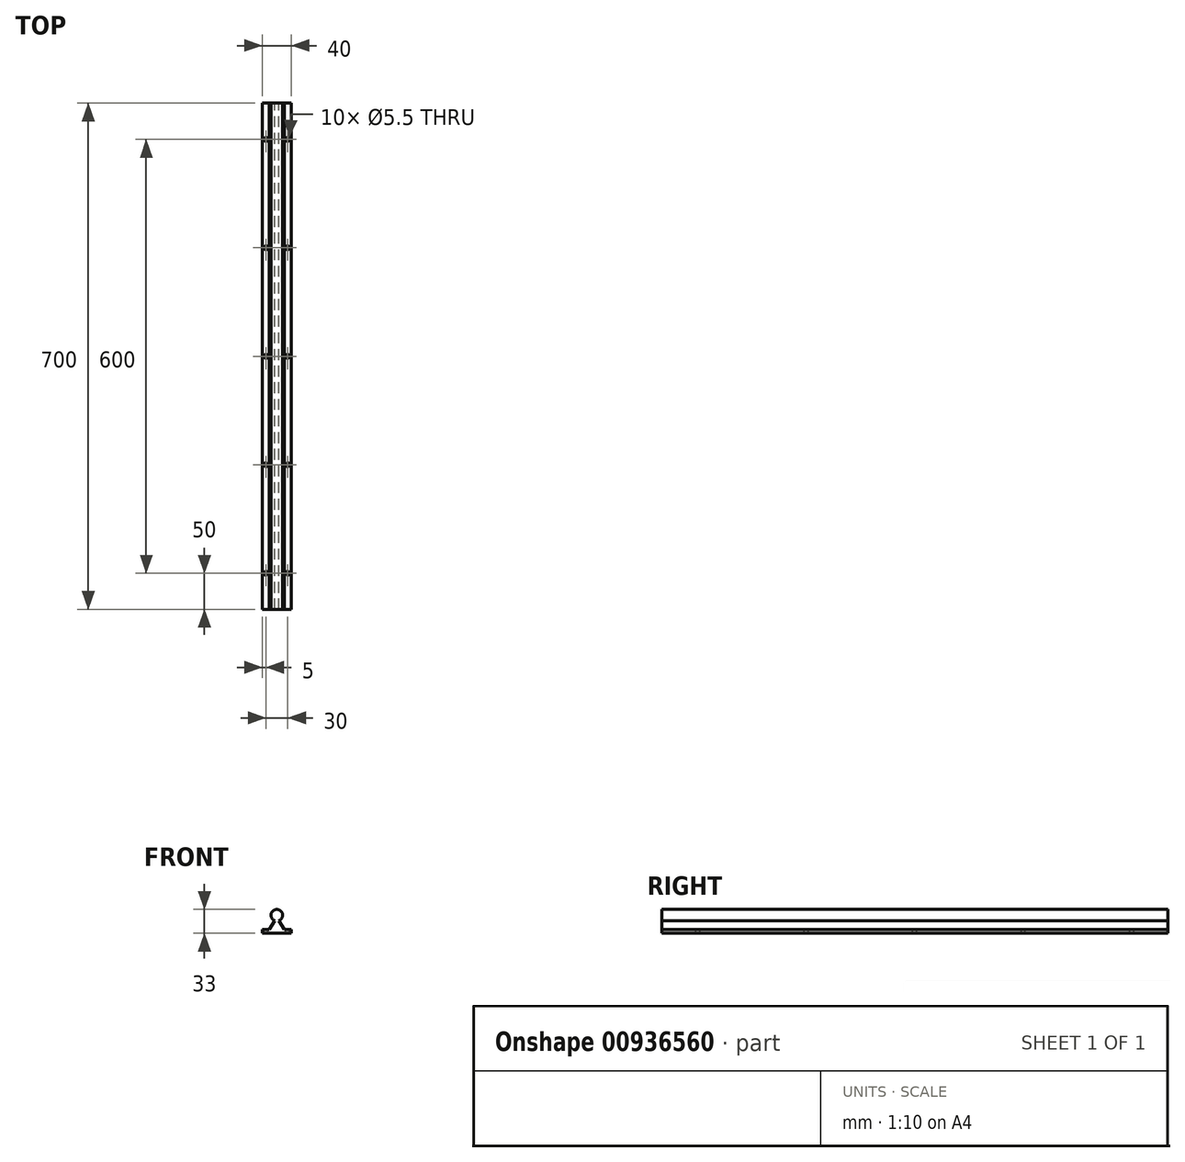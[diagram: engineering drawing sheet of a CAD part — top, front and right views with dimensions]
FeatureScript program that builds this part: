
annotation { "Feature Type Name" : "Feature", "Feature Type Description" : "" }
export const myFeature = defineFeature(function(context is Context, id is Id, definition is map)
    precondition{}
    {
        {
            var Q0;
            Q0=qCreatedBy(makeId("Front.planeOp"),FACE);
            var sketch = newSketch(context, id + "F0", { "sketchPlane" : qUnion([Q0])});
            skLineSegment(sketch, "E0", {"start": v(-56.48, 0) * mm, "end": v(69.29, 0) * mm, "construction": true});
            skLineSegment(sketch, "E1", {"start": v(0, 0) * mm, "end": v(-20, 0) * mm});
            skLineSegment(sketch, "E2", {"start": v(-20, 0) * mm, "end": v(-20, 5) * mm});
            skLineSegment(sketch, "E3", {"start": v(-20, 5) * mm, "end": v(-10.15, 5) * mm});
            skArc(sketch, "E4", {"start": v(3, 17.58) * mm, "mid": v(0, 33) * mm, "end": v(-3, 17.58) * mm});
            skLineSegment(sketch, "E5", {"start": v(-10.15, 5) * mm, "end": v(-3, 17.58) * mm});
            skLineSegment(sketch, "E6", {"start": v(0, 27.09) * mm, "end": v(0, 0) * mm, "construction": true});
            skLineSegment(sketch, "E7.MirrorCS", {"start": v(0, 0) * mm, "end": v(20, 0) * mm});
            skLineSegment(sketch, "E8.MirrorCS", {"start": v(20, 0) * mm, "end": v(20, 5) * mm});
            skLineSegment(sketch, "E9.MirrorCS", {"start": v(10.15, 5) * mm, "end": v(3, 17.58) * mm});
            skLineSegment(sketch, "E10.MirrorCS", {"start": v(20, 5) * mm, "end": v(10.15, 5) * mm});
            skSolve(sketch);
        }
        {
            var Q0;
            Q0=makeQuery(id+"F0.imprint","IMPRINT",FACE,{"disambiguationData":[TD([[makeQuery(id+"F0.imprint","IMPRINT",EDGE,{"derivedFrom":sQuery(id+"F0.wireOp",EDGE,"E1")}),-1.0]])]});
            extrude(context, id + "F1", {"entities" : qUnion([Q0]), "depth" : 700 * mm, "offsetDistance" : 25 * mm});
        }
        {
            var Q0;
            Q0=makeQuery(id+"F1.opExtrude","SWEPT_FACE",FACE,{"disambiguationData":[OSD([sQuery(id+"F0.wireOp",EDGE,"E1"),sQuery(id+"F0.wireOp",EDGE,"E7.MirrorCS")])]});
            var sketch = newSketch(context, id + "F2", { "sketchPlane" : qUnion([Q0])});
            skLineSegment(sketch, "E11", {"start": v(0, 0) * mm, "end": v(0, 41.99) * mm, "construction": true});
            skPoint(sketch, "E12", {"position": v(-15, 50) * mm});
            skPoint(sketch, "E13.MirrorP", {"position": v(15, 50) * mm});
            skPoint(sketch, "E14.0.1.0", {"position": v(-15, 200) * mm});
            skPoint(sketch, "E14.0.1.1", {"position": v(15, 200) * mm});
            skPoint(sketch, "E14.0.2.0", {"position": v(-15, 350) * mm});
            skPoint(sketch, "E14.0.2.1", {"position": v(15, 350) * mm});
            skPoint(sketch, "E14.0.3.0", {"position": v(-15, 500) * mm});
            skPoint(sketch, "E14.0.3.1", {"position": v(15, 500) * mm});
            skPoint(sketch, "E14.0.4.0", {"position": v(-15, 650) * mm});
            skPoint(sketch, "E14.0.4.1", {"position": v(15, 650) * mm});
            skLineSegment(sketch, "E14.direction1", {"start": v(-15, 50) * mm, "end": v(14, 50) * mm, "construction": true});
            skLineSegment(sketch, "E14.direction2", {"start": v(-15, 50) * mm, "end": v(-15, 200) * mm, "construction": true});
            skSolve(sketch);
        }
        {
            var Q0;
            Q0=sQuery(id+"F2.wireOp",VERTEX,"E12");
            var Q1;
            Q1=sQuery(id+"F2.wireOp",VERTEX,"E13.MirrorP");
            var Q2;
            Q2=sQuery(id+"F2.wireOp",VERTEX,"E14.0.1.0");
            var Q3;
            Q3=sQuery(id+"F2.wireOp",VERTEX,"E14.0.1.1");
            var Q4;
            Q4=sQuery(id+"F2.wireOp",VERTEX,"E14.0.2.0");
            var Q5;
            Q5=sQuery(id+"F2.wireOp",VERTEX,"E14.0.2.1");
            var Q6;
            Q6=sQuery(id+"F2.wireOp",VERTEX,"E14.0.3.0");
            var Q7;
            Q7=sQuery(id+"F2.wireOp",VERTEX,"E14.0.3.1");
            var Q8;
            Q8=sQuery(id+"F2.wireOp",VERTEX,"E14.0.4.0");
            var Q9;
            Q9=sQuery(id+"F2.wireOp",VERTEX,"E14.0.4.1");
            var Q10;
            Q10=makeQuery(id+"F1.opExtrude","SWEPT_BODY",BODY,{"disambiguationData":[OSD([sQuery(id+"F0.wireOp",EDGE,"E1"),sQuery(id+"F0.wireOp",EDGE,"E2"),sQuery(id+"F0.wireOp",EDGE,"E3"),sQuery(id+"F0.wireOp",EDGE,"E4"),sQuery(id+"F0.wireOp",EDGE,"E5"),sQuery(id+"F0.wireOp",EDGE,"E7.MirrorCS"),sQuery(id+"F0.wireOp",EDGE,"E8.MirrorCS"),sQuery(id+"F0.wireOp",EDGE,"E9.MirrorCS"),sQuery(id+"F0.wireOp",EDGE,"E10.MirrorCS")])]});
            hole(context, id + "F3", {"style" : HoleStyle.SIMPLE, "endStyle" : HoleEndStyle.THROUGH, "standardTappedOrClearance" : lookupTablePath({ "fit" : "Normal", "standard" : "ISO", "size" : "M5", "type" : "Clearance" }), "standardBlindInLast" : lookupTablePath({ "fit" : "Standard", "standard" : "ISO", "size" : "M5", "type" : "Clearance" }), "holeDiameter" : 5.5 * mm, "majorDiameter" : 5 * mm, "isTappedThrough" : true, "tappedDepth" : 12 * mm, "tapClearance" : 3, "locations" : qUnion([Q0, Q1, Q2, Q3, Q4, Q5, Q6, Q7, Q8, Q9]), "scope" : qUnion([Q10]), "startStyle" : HoleStartStyle.PART});
        }
    });
